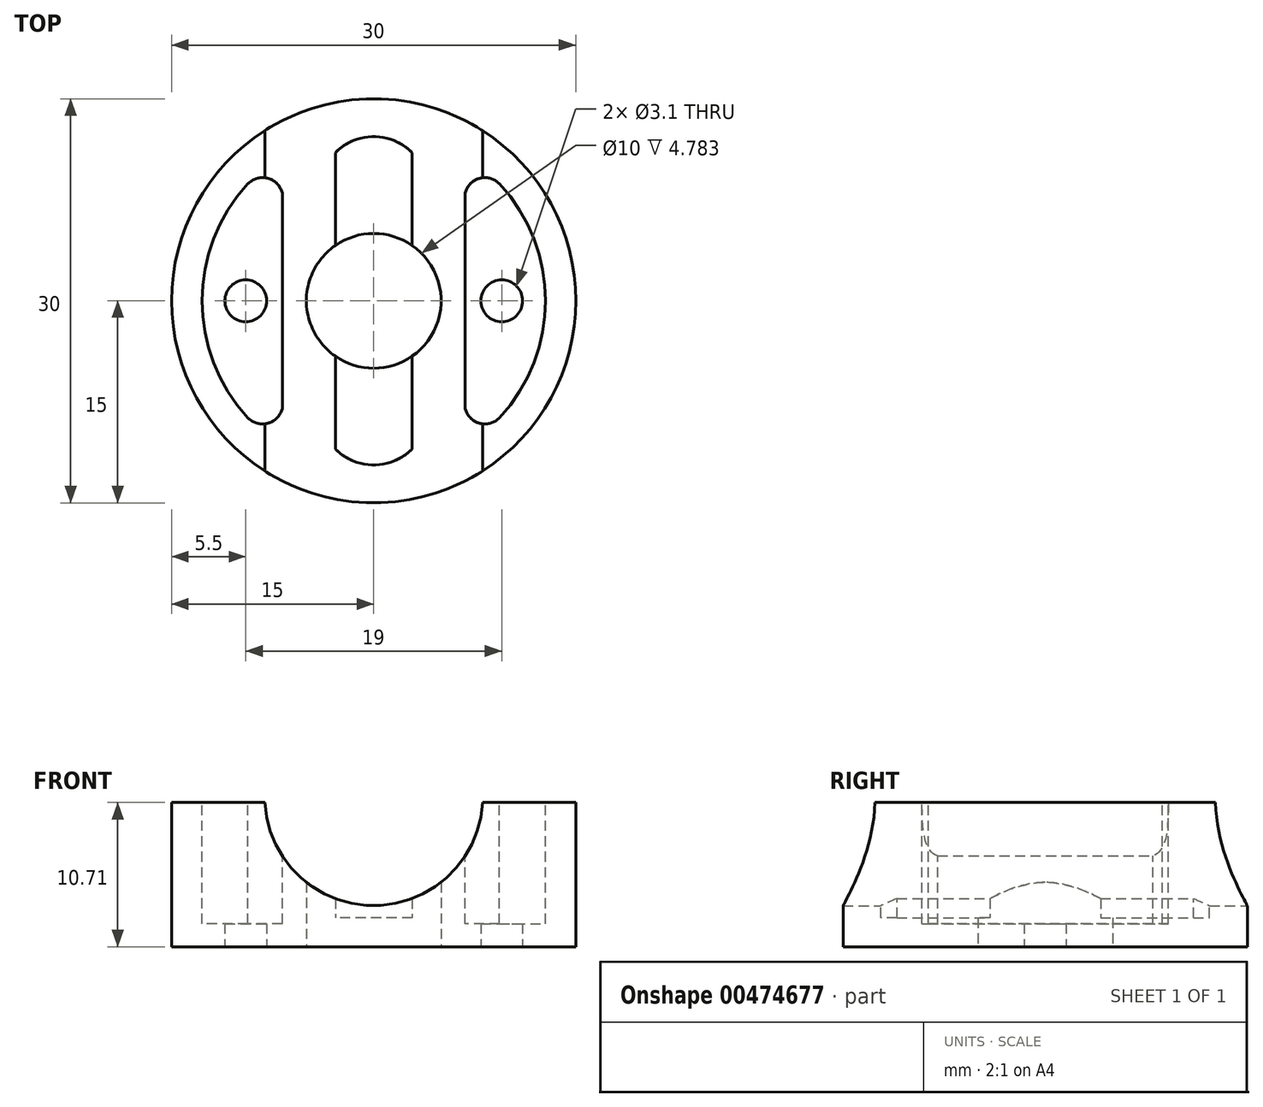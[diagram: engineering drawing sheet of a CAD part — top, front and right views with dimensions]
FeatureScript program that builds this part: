
annotation { "Feature Type Name" : "Feature", "Feature Type Description" : "" }
export const myFeature = defineFeature(function(context is Context, id is Id, definition is map)
    precondition{}
    {
        {
            var Q0;
            Q0=qCreatedBy(makeId("Front.planeOp"),FACE);
            var sketch = newSketch(context, id + "F0", { "sketchPlane" : qUnion([Q0])});
            skLineSegment(sketch, "E0.bottom", {"start": v(15, -6) * mm, "end": v(-15, -6) * mm});
            skLineSegment(sketch, "E0.top", {"start": v(15, 6) * mm, "end": v(-15, 6) * mm});
            skLineSegment(sketch, "E0.left", {"start": v(15, -6) * mm, "end": v(15, 6) * mm});
            skLineSegment(sketch, "E0.right", {"start": v(-15, -6) * mm, "end": v(-15, 6) * mm});
            skPoint(sketch, "E0.middle", {"position": v(0, 0) * mm});
            skArc(sketch, "E1", {"start": v(-8.1, 6) * mm, "mid": v(0, -2.1) * mm, "end": v(8.1, 6) * mm});
            skLineSegment(sketch, "E2", {"start": v(-15, 5.56) * mm, "end": v(15, 5.56) * mm});
            skLineSegment(sketch, "E3", {"start": v(0, -2.1) * mm, "end": v(0, -6) * mm});
            skSolve(sketch);
        }
        {
            var Q0;
            {var subQ5=sQuery(id+"F0.wireOp",EDGE,"E3");Q0=makeQuery(id+"F0.imprint","IMPRINT",FACE,{"disambiguationData":[TD([[makeQuery(id+"F0.imprint","IMPRINT",EDGE,{"derivedFrom":subQ5}),-1.0]])]});}
            var Q1;
            {var subQ0=sQuery(id+"F0.wireOp",EDGE,"E3");Q1=makeQuery(id+"F0.imprint","IMPRINT",FACE,{"disambiguationData":[TD([[makeQuery(id+"F0.imprint","IMPRINT",EDGE,{"derivedFrom":subQ0}),1.0]])]});}
            extrude(context, id + "F1", {"entities" : qUnion([Q0, Q1]), "endBound" : BoundingType.SYMMETRIC, "depth" : 30 * mm});
        }
        {
            var Q0;
            {var subQ0=sQuery(id+"F0.wireOp",EDGE,"E2");Q0=makeQuery(id+"F1.opExtrude","SWEPT_FACE",FACE,{"disambiguationData":[OSD([subQ0]),TDD([makeQuery(id+"F0.imprint","IMPRINT",EDGE,{"disambiguationData":[TD([[makeQuery(id+"F0.imprint","INTERSECT",VERTEX,{"derivedFrom":[sQuery(id+"F0.wireOp",EDGE,"E0.right"),subQ0]}),-1.0]])],"derivedFrom":subQ0})])]});}
            var sketch = newSketch(context, id + "F2", { "sketchPlane" : qUnion([Q0])});
            skCircle(sketch, "E4", {"center": v(0, 0) * mm, "radius": 15 * mm});
            skLineSegment(sketch, "E5.bottom", {"start": v(15, -15) * mm, "end": v(-15, -15) * mm});
            skLineSegment(sketch, "E5.top", {"start": v(15, 15) * mm, "end": v(-15, 15) * mm});
            skLineSegment(sketch, "E5.left", {"start": v(15, -15) * mm, "end": v(15, 15) * mm});
            skLineSegment(sketch, "E5.right", {"start": v(-15, -15) * mm, "end": v(-15, 15) * mm});
            skSolve(sketch);
        }
        {
            var Q0;
            {var subQ0=sQuery(id+"F2.wireOp",EDGE,"E5.right");var subQ7=sQuery(id+"F2.wireOp",EDGE,"E5.bottom");var subQ8=makeQuery(id+"F2.imprint","INTERSECT",VERTEX,{"derivedFrom":[subQ7,subQ0]});Q0=makeQuery(id+"F2.imprint","IMPRINT",FACE,{"disambiguationData":[TD([[makeQuery(id+"F2.imprint","IMPRINT",EDGE,{"disambiguationData":[TD([[subQ8,-1.0]])],"derivedFrom":subQ0}),-1.0]])]});}
            var Q1;
            {var subQ0=sQuery(id+"F2.wireOp",EDGE,"E5.bottom");var subQ1=sQuery(id+"F2.wireOp",EDGE,"E4");var subQ2=makeQuery(id+"F2.imprint","INTERSECT",VERTEX,{"derivedFrom":[subQ1,subQ0]});Q1=makeQuery(id+"F2.imprint","IMPRINT",FACE,{"disambiguationData":[TD([[makeQuery(id+"F2.imprint","IMPRINT",EDGE,{"disambiguationData":[TD([[subQ2,1.0]])],"derivedFrom":subQ1}),-1.0]])]});}
            var Q2;
            {var subQ0=sQuery(id+"F2.wireOp",EDGE,"E5.right");var subQ7=sQuery(id+"F2.wireOp",EDGE,"E5.top");var subQ8=makeQuery(id+"F2.imprint","INTERSECT",VERTEX,{"derivedFrom":[subQ7,subQ0]});Q2=makeQuery(id+"F2.imprint","IMPRINT",FACE,{"disambiguationData":[TD([[makeQuery(id+"F2.imprint","IMPRINT",EDGE,{"disambiguationData":[TD([[subQ8,1.0]])],"derivedFrom":subQ0}),-1.0]])]});}
            var Q3;
            {var subQ0=sQuery(id+"F2.wireOp",EDGE,"E5.top");var subQ1=sQuery(id+"F2.wireOp",EDGE,"E4");var subQ2=makeQuery(id+"F2.imprint","INTERSECT",VERTEX,{"derivedFrom":[subQ1,subQ0]});Q3=makeQuery(id+"F2.imprint","IMPRINT",FACE,{"disambiguationData":[TD([[makeQuery(id+"F2.imprint","IMPRINT",EDGE,{"disambiguationData":[TD([[subQ2,-1.0]])],"derivedFrom":subQ1}),-1.0]])]});}
            var Q4;
            {var subQ0=sQuery(id+"F2.wireOp",EDGE,"E5.top");var subQ1=sQuery(id+"F2.wireOp",EDGE,"E4");var subQ2=makeQuery(id+"F2.imprint","INTERSECT",VERTEX,{"derivedFrom":[subQ1,subQ0]});Q4=makeQuery(id+"F2.imprint","IMPRINT",FACE,{"disambiguationData":[TD([[makeQuery(id+"F2.imprint","IMPRINT",EDGE,{"disambiguationData":[TD([[subQ2,1.0]])],"derivedFrom":subQ1}),-1.0]])]});}
            var Q5;
            {var subQ0=sQuery(id+"F2.wireOp",EDGE,"E5.left");var subQ1=sQuery(id+"F2.wireOp",EDGE,"E4");var subQ2=makeQuery(id+"F2.imprint","INTERSECT",VERTEX,{"derivedFrom":[subQ1,subQ0]});Q5=makeQuery(id+"F2.imprint","IMPRINT",FACE,{"disambiguationData":[TD([[makeQuery(id+"F2.imprint","IMPRINT",EDGE,{"disambiguationData":[TD([[subQ2,1.0]])],"derivedFrom":subQ1}),-1.0]])]});}
            extrude(context, id + "F3", {"entities" : qUnion([Q0, Q1, Q2, Q3, Q4, Q5]), "operationType" : NewBodyOperationType.REMOVE, "oppositeDirection" : true, "depth" : 12 * mm});
        }
        {
            var Q0;
            {var subQ0=sQuery(id+"F0.wireOp",EDGE,"E2");Q0=makeQuery(id+"F1.opExtrude","SWEPT_FACE",FACE,{"disambiguationData":[OSD([subQ0]),TDD([makeQuery(id+"F0.imprint","IMPRINT",EDGE,{"disambiguationData":[TD([[makeQuery(id+"F0.imprint","INTERSECT",VERTEX,{"derivedFrom":[sQuery(id+"F0.wireOp",EDGE,"E0.left"),subQ0]}),1.0]])],"derivedFrom":subQ0})])]});}
            var sketch = newSketch(context, id + "F4", { "sketchPlane" : qUnion([Q0])});
            skCircle(sketch, "E6", {"center": v(0, 0) * mm, "radius": 12.75 * mm});
            skLineSegment(sketch, "E7", {"start": v(-6.8, 10.8) * mm, "end": v(-6.8, -10.8) * mm});
            skLineSegment(sketch, "E8", {"start": v(6.8, 10.8) * mm, "end": v(6.8, -10.8) * mm});
            skArc(sketch, "E9", {"start": v(-6.8, 8) * mm, "mid": v(-7.86, 9.1) * mm, "end": v(-9.33, 8.69) * mm});
            skArc(sketch, "E10", {"start": v(-9.33, -8.69) * mm, "mid": v(-7.86, -9.1) * mm, "end": v(-6.8, -8) * mm});
            skArc(sketch, "E11", {"start": v(6.8, -8) * mm, "mid": v(7.86, -9.1) * mm, "end": v(9.33, -8.69) * mm});
            skArc(sketch, "E12", {"start": v(9.33, 8.69) * mm, "mid": v(7.86, 9.1) * mm, "end": v(6.8, 8) * mm});
            skSolve(sketch);
        }
        {
            var Q0;
            {var subQ0=sQuery(id+"F4.wireOp",EDGE,"E9");Q0=makeQuery(id+"F4.imprint","IMPRINT",FACE,{"disambiguationData":[TD([[makeQuery(id+"F4.imprint","IMPRINT",EDGE,{"derivedFrom":subQ0}),1.0]])]});}
            var Q1;
            {var subQ0=sQuery(id+"F4.wireOp",EDGE,"E11");var subQ1=sQuery(id+"F4.wireOp",EDGE,"E6");var subQ2=makeQuery(id+"F4.imprint","INTERSECT",VERTEX,{"derivedFrom":[subQ1,subQ0]});Q1=makeQuery(id+"F4.imprint","IMPRINT",FACE,{"disambiguationData":[TD([[makeQuery(id+"F4.imprint","IMPRINT",EDGE,{"disambiguationData":[TD([[subQ2,-1.0]])],"derivedFrom":subQ1}),1.0]])]});}
            var Q2;
            {var subQ0=sQuery(id+"F4.wireOp",EDGE,"E11");var subQ1=sQuery(id+"F4.wireOp",EDGE,"E8");var subQ2=makeQuery(id+"F4.imprint","INTERSECT",VERTEX,{"derivedFrom":[subQ1,subQ0]});Q2=makeQuery(id+"F4.imprint","IMPRINT",FACE,{"disambiguationData":[TD([[makeQuery(id+"F4.imprint","IMPRINT",EDGE,{"disambiguationData":[TD([[subQ2,1.0]])],"derivedFrom":subQ1}),1.0]])]});}
            extrude(context, id + "F5", {"entities" : qUnion([Q0, Q1, Q2]), "operationType" : NewBodyOperationType.REMOVE, "oppositeDirection" : true, "depth" : 9 * mm});
        }
        {
            var Q0;
            Q0=makeQuery(id+"F1.opExtrude","SWEPT_FACE",FACE,{"disambiguationData":[OSD([sQuery(id+"F0.wireOp",EDGE,"E0.bottom")])]});
            var sketch = newSketch(context, id + "F6", { "sketchPlane" : qUnion([Q0])});
            skCircle(sketch, "E13", {"center": v(0, 0) * mm, "radius": 5 * mm});
            skSolve(sketch);
        }
        {
            var Q0;
            Q0=makeQuery(id+"F6.imprint","IMPRINT",FACE,{"disambiguationData":[TD([[makeQuery(id+"F6.imprint","IMPRINT",EDGE,{"derivedFrom":sQuery(id+"F6.wireOp",EDGE,"E13")}),1.0]])]});
            extrude(context, id + "F7", {"entities" : qUnion([Q0]), "operationType" : NewBodyOperationType.REMOVE, "oppositeDirection" : true, "depth" : 12 * mm});
        }
        {
            var Q0;
            Q0=makeQuery(id+"F1.opExtrude","SWEPT_FACE",FACE,{"disambiguationData":[OSD([sQuery(id+"F0.wireOp",EDGE,"E0.bottom")])]});
            var sketch = newSketch(context, id + "F8", { "sketchPlane" : qUnion([Q0])});
            skCircle(sketch, "E14", {"center": v(9.5, 0) * mm, "radius": 1.55 * mm});
            skCircle(sketch, "E15", {"center": v(-9.5, 0) * mm, "radius": 1.55 * mm});
            skSolve(sketch);
        }
        {
            var Q0;
            Q0=makeQuery(id+"F8.imprint","IMPRINT",FACE,{"disambiguationData":[TD([[makeQuery(id+"F8.imprint","IMPRINT",EDGE,{"derivedFrom":sQuery(id+"F8.wireOp",EDGE,"E15")}),1.0]])]});
            var Q1;
            Q1=makeQuery(id+"F8.imprint","IMPRINT",FACE,{"disambiguationData":[TD([[makeQuery(id+"F8.imprint","IMPRINT",EDGE,{"derivedFrom":sQuery(id+"F8.wireOp",EDGE,"E14")}),1.0]])]});
            extrude(context, id + "F9", {"entities" : qUnion([Q0, Q1]), "operationType" : NewBodyOperationType.REMOVE, "oppositeDirection" : true, "depth" : 12 * mm});
        }
        {
            var Q0;
            Q0=qCreatedBy(makeId("Top.planeOp"),FACE);
            var sketch = newSketch(context, id + "F10", { "sketchPlane" : qUnion([Q0])});
            skLineSegment(sketch, "E16.bottom", {"start": v(2.85, -11) * mm, "end": v(-2.85, -11) * mm});
            skLineSegment(sketch, "E16.top", {"start": v(2.85, 11) * mm, "end": v(-2.85, 11) * mm});
            skLineSegment(sketch, "E16.left", {"start": v(2.85, -11) * mm, "end": v(2.85, 11) * mm});
            skLineSegment(sketch, "E16.right", {"start": v(-2.85, -11) * mm, "end": v(-2.85, 11) * mm});
            skPoint(sketch, "E16.middle", {"position": v(0, 0) * mm});
            skArc(sketch, "E17", {"start": v(2.85, 11) * mm, "mid": v(0, 12.2) * mm, "end": v(-2.85, 11) * mm});
            skArc(sketch, "E18", {"start": v(-2.85, -11) * mm, "mid": v(0, -12.2) * mm, "end": v(2.85, -11) * mm});
            skSolve(sketch);
        }
        {
            var Q0;
            Q0=makeQuery(id+"F10.imprint","IMPRINT",FACE,{"disambiguationData":[TD([[makeQuery(id+"F10.imprint","IMPRINT",EDGE,{"derivedFrom":sQuery(id+"F10.wireOp",EDGE,"E16.bottom")}),-1.0]])]});
            var Q1;
            Q1=makeQuery(id+"F10.imprint","IMPRINT",FACE,{"disambiguationData":[TD([[makeQuery(id+"F10.imprint","IMPRINT",EDGE,{"derivedFrom":sQuery(id+"F10.wireOp",EDGE,"E16.top")}),-1.0]])]});
            var Q2;
            Q2=makeQuery(id+"F10.imprint","IMPRINT",FACE,{"disambiguationData":[TD([[makeQuery(id+"F10.imprint","IMPRINT",EDGE,{"derivedFrom":sQuery(id+"F10.wireOp",EDGE,"E16.bottom")}),1.0]])]});
            extrude(context, id + "F11", {"entities" : qUnion([Q0, Q1, Q2]), "operationType" : NewBodyOperationType.REMOVE, "oppositeDirection" : true, "depth" : 3 * mm});
        }
        {
            var Q0;
            Q0=makeQuery(id+"F1.opExtrude","SWEPT_FACE",FACE,{"disambiguationData":[OSD([sQuery(id+"F0.wireOp",EDGE,"E0.bottom")])]});
            var Q1;
            Q1=makeQuery(id+"F1.opExtrude","SWEPT_FACE",FACE,{"disambiguationData":[OSD([sQuery(id+"F0.wireOp",EDGE,"E0.bottom")])]});
            var sketch = newSketch(context, id + "F12", { "sketchPlane" : qUnion([Q0, Q1])});
            skCircle(sketch, "E19", {"center": v(0, 0) * mm, "radius": 15 * mm});
            skSolve(sketch);
        }
        {
            var Q0;
            Q0=makeQuery(id+"F12.imprint","IMPRINT",FACE,{"disambiguationData":[TD([[makeQuery(id+"F12.imprint","IMPRINT",EDGE,{"derivedFrom":sQuery(id+"F12.wireOp",EDGE,"E19")}),1.0]])]});
            extrude(context, id + "F13", {"entities" : qUnion([Q0]), "operationType" : NewBodyOperationType.REMOVE, "oppositeDirection" : true, "depth" : 0.85 * mm});
        }
    });
